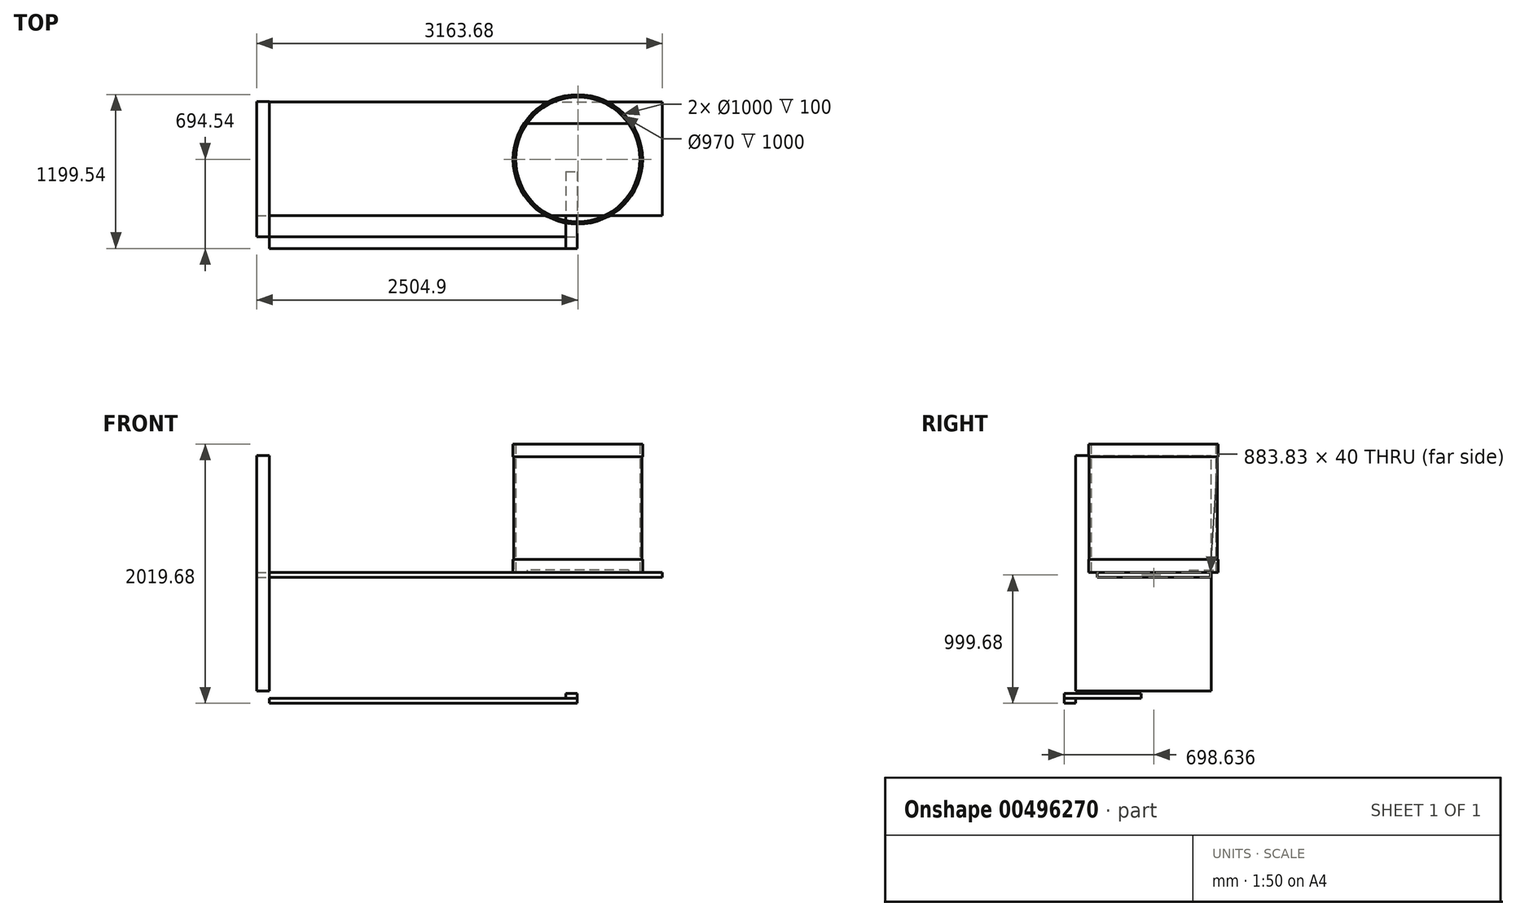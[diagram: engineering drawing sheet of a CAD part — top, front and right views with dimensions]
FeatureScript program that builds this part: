
annotation { "Feature Type Name" : "Feature", "Feature Type Description" : "" }
export const myFeature = defineFeature(function(context is Context, id is Id, definition is map)
    precondition{}
    {
        {
            var Q0;
            Q0=qCreatedBy(makeId("Top.planeOp"),FACE);
            var sketch = newSketch(context, id + "F0", { "sketchPlane" : qUnion([Q0])});
            skCircle(sketch, "E0", {"center": v(0, 0) * mm, "radius": 500 * mm});
            skSolve(sketch);
        }
        {
            var Q0;
            Q0=qSketchRegion(id+"F0",true);
            var sketch = newSketch(context, id + "F1", { "sketchPlane" : qUnion([Q0])});
            skCircle(sketch, "E1.0", {"center": v(0, 0) * mm, "radius": 485 * mm});
            skSolve(sketch);
        }
        {
            var Q0;
            Q0=qSketchRegion(id+"F0",true);
            var sketch = newSketch(context, id + "F2", { "sketchPlane" : qUnion([Q0])});
            skSolve(sketch);
        }
        {
            var Q0;
            Q0=makeQuery(id+"F1.imprint","IMPRINT",FACE,{"disambiguationData":[TD([[makeQuery(id+"F1.imprint","IMPRINT",EDGE,{"derivedFrom":sQuery(id+"F1.wireOp",EDGE,"E1.0")}),-1.0]])]});
            extrude(context, id + "F3", {"entities" : qUnion([Q0]), "depth" : 1000 * mm});
        }
        {
            var Q0;
            Q0=makeQuery(id+"F3.opExtrude","CAP_FACE",FACE,{"disambiguationData":[OSD([sQuery(id+"F0.wireOp",EDGE,"E0"),sQuery(id+"F1.wireOp",EDGE,"E1.0")])],"isStart":false});
            var sketch = newSketch(context, id + "F4", { "sketchPlane" : qUnion([Q0])});
            skCircle(sketch, "E2.0", {"center": v(0, 0) * mm, "radius": 505 * mm});
            skSolve(sketch);
        }
        {
            var Q0;
            Q0=makeQuery(id+"F4.imprint","IMPRINT",FACE,{"disambiguationData":[TD([[makeQuery(id+"F4.imprint","IMPRINT",EDGE,{"derivedFrom":sQuery(id+"F4.wireOp",EDGE,"E2.0")}),1.0]])]});
            var Q1;
            Q1=sQuery(id+"F4.wireOp",EDGE,"E2.0");
            extrude(context, id + "F5", {"entities" : qUnion([Q0]), "surfaceEntities" : qUnion([Q1]), "oppositeDirection" : true, "depth" : 100 * mm});
        }
        {
            var Q0;
            Q0=qSketchRegion(id+"F0",true);
            var sketch = newSketch(context, id + "F6", { "sketchPlane" : qUnion([Q0])});
            skCircle(sketch, "E3.0", {"center": v(0, 0) * mm, "radius": 505 * mm});
            skSolve(sketch);
        }
        {
            var Q0;
            Q0=makeQuery(id+"F6.imprint","IMPRINT",FACE,{"disambiguationData":[TD([[makeQuery(id+"F6.imprint","IMPRINT",EDGE,{"derivedFrom":sQuery(id+"F6.wireOp",EDGE,"E3.0")}),1.0]])]});
            var Q1;
            Q1=sQuery(id+"F6.wireOp",EDGE,"E3.0");
            var Q2;
            Q2=sQuery(id+"F0.wireOp",EDGE,"E0");
            extrude(context, id + "F7", {"entities" : qUnion([Q0]), "surfaceEntities" : qUnion([Q1, Q2]), "depth" : 100 * mm});
        }
        {
            var Q0;
            Q0=makeQuery(id+"F2.imprint","IMPRINT",FACE,{"disambiguationData":[TD([[makeQuery(id+"F2.imprint","IMPRINT",EDGE,{"derivedFrom":makeQuery(id+"F0.imprint","IMPRINT",EDGE,{"derivedFrom":sQuery(id+"F0.wireOp",EDGE,"E0")})}),1.0]])]});
            var sketch = newSketch(context, id + "F8", { "sketchPlane" : qUnion([Q0])});
            skLineSegment(sketch, "E4.0", {"start": v(-670.82, -280) * mm, "end": v(736.95, -280) * mm, "construction": true});
            skLineSegment(sketch, "E5.0", {"start": v(-280, 280) * mm, "end": v(736.95, 280) * mm, "construction": true});
            skLineSegment(sketch, "E6.0", {"start": v(-280, 280) * mm, "end": v(-280, -540.65) * mm, "construction": true});
            skLineSegment(sketch, "E7.0", {"start": v(280, 677.08) * mm, "end": v(280, -540.65) * mm, "construction": true});
            skCircle(sketch, "E8", {"center": v(392.31, 0) * mm, "radius": 25 * mm, "construction": true});
            skCircle(sketch, "E9", {"center": v(-397.36, 0) * mm, "radius": 25 * mm, "construction": true});
            skPoint(sketch, "E10.orphan", {"position": v(-670.82, 0) * mm});
            skPoint(sketch, "E11.orphan", {"position": v(0, 677.08) * mm});
            skLineSegment(sketch, "E12", {"start": v(-280, 210.88) * mm, "end": v(-280, 476.58) * mm});
            skLineSegment(sketch, "E13", {"start": v(-280, 280) * mm, "end": v(-559.63, 280) * mm});
            skSolve(sketch);
        }
        {
            var Q0;
            {var subQ0=sQuery(id+"F8.wireOp",EDGE,"E13");var subQ1=sQuery(id+"F8.wireOp",EDGE,"E12");var subQ2=makeQuery(id+"F8.imprint","INTERSECT",VERTEX,{"derivedFrom":[subQ1,subQ0]});Q0=makeQuery(id+"F8.imprint","IMPRINT",FACE,{"disambiguationData":[TD([[makeQuery(id+"F8.imprint","IMPRINT",EDGE,{"disambiguationData":[TD([[subQ2,-1.0]])],"derivedFrom":subQ1}),-1.0]])]});}
            var sketch = newSketch(context, id + "F9", { "sketchPlane" : qUnion([Q0])});
            skLineSegment(sketch, "E14", {"start": v(737.94, 279) * mm, "end": v(-365.76, 279) * mm});
            skLineSegment(sketch, "E15", {"start": v(-365.76, 279) * mm, "end": v(-460.28, 279) * mm});
            skArc(sketch, "E16", {"start": v(396.86, 279) * mm, "mid": v(0, 485.12) * mm, "end": v(-396.86, 279) * mm});
            skSolve(sketch);
        }
        {
            var Q0;
            Q0=qSketchRegion(id+"F9",true);
            extrude(context, id + "F10", {"entities" : qUnion([Q0]), "depth" : 20 * mm});
        }
        {
            var Q0;
            Q0=makeQuery(id+"F2.imprint","IMPRINT",FACE,{"disambiguationData":[TD([[makeQuery(id+"F2.imprint","IMPRINT",EDGE,{"derivedFrom":makeQuery(id+"F0.imprint","IMPRINT",EDGE,{"derivedFrom":sQuery(id+"F0.wireOp",EDGE,"E0")})}),1.0]])]});
            var sketch = newSketch(context, id + "F11", { "sketchPlane" : qUnion([Q0])});
            skLineSegment(sketch, "E17.bottom", {"start": v(-2404.9, -437.82) * mm, "end": v(658.78, -437.82) * mm});
            skLineSegment(sketch, "E17.top", {"start": v(-2404.9, 446) * mm, "end": v(658.78, 446) * mm});
            skLineSegment(sketch, "E17.left", {"start": v(-2404.9, -437.82) * mm, "end": v(-2404.9, 446) * mm});
            skLineSegment(sketch, "E17.right", {"start": v(658.78, -437.82) * mm, "end": v(658.78, 446) * mm});
            skSolve(sketch);
        }
        {
            var Q0;
            Q0=qSketchRegion(id+"F11",true);
            extrude(context, id + "F12", {"entities" : qUnion([Q0]), "oppositeDirection" : true, "depth" : 40 * mm});
        }
        {
            var Q0;
            Q0=makeQuery(id+"F12.opExtrude","SWEPT_FACE",FACE,{"disambiguationData":[OSD([sQuery(id+"F11.wireOp",EDGE,"E17.left")])]});
            var sketch = newSketch(context, id + "F13", { "sketchPlane" : qUnion([Q0])});
            skLineSegment(sketch, "E18.bottom", {"start": v(604.54, -923.26) * mm, "end": v(-449.95, -923.26) * mm});
            skLineSegment(sketch, "E18.top", {"start": v(604.54, 909.63) * mm, "end": v(-449.95, 909.63) * mm});
            skLineSegment(sketch, "E18.left", {"start": v(604.54, -923.26) * mm, "end": v(604.54, 909.63) * mm});
            skLineSegment(sketch, "E18.right", {"start": v(-449.95, -923.26) * mm, "end": v(-449.95, 909.63) * mm});
            skSolve(sketch);
        }
        {
            var Q0;
            Q0=makeQuery(id+"F13.imprint","IMPRINT",FACE,{"disambiguationData":[TD([[makeQuery(id+"F13.imprint","IMPRINT",EDGE,{"derivedFrom":sQuery(id+"F13.wireOp",EDGE,"E18.bottom")}),-1.0]])]});
            extrude(context, id + "F14", {"entities" : qUnion([Q0]), "depth" : 100 * mm});
        }
        {
            var Q0;
            Q0=makeQuery(id+"F14.opExtrude","SWEPT_FACE",FACE,{"disambiguationData":[OSD([sQuery(id+"F13.wireOp",EDGE,"E18.left")])]});
            var sketch = newSketch(context, id + "F15", { "sketchPlane" : qUnion([Q0])});
            skLineSegment(sketch, "E19.bottom", {"start": v(-2404.9, -981.68) * mm, "end": v(-4.9, -981.68) * mm});
            skLineSegment(sketch, "E19.top", {"start": v(-2404.9, -1019.68) * mm, "end": v(-4.9, -1019.68) * mm});
            skLineSegment(sketch, "E19.left", {"start": v(-2404.9, -981.68) * mm, "end": v(-2404.9, -1019.68) * mm});
            skLineSegment(sketch, "E19.right", {"start": v(-4.9, -981.68) * mm, "end": v(-4.9, -1019.68) * mm});
            skSolve(sketch);
        }
        {
            var Q0;
            Q0=qSketchRegion(id+"F15",true);
            extrude(context, id + "F16", {"entities" : qUnion([Q0]), "depth" : 90 * mm});
        }
        {
            var Q0;
            Q0=makeQuery(id+"F16.opExtrude","CAP_FACE",FACE,{"disambiguationData":[OSD([sQuery(id+"F15.wireOp",EDGE,"E19.bottom"),sQuery(id+"F15.wireOp",EDGE,"E19.top"),sQuery(id+"F15.wireOp",EDGE,"E19.left"),sQuery(id+"F15.wireOp",EDGE,"E19.right")])],"isStart":false});
            var sketch = newSketch(context, id + "F17", { "sketchPlane" : qUnion([Q0])});
            skLineSegment(sketch, "E20.bottom", {"start": v(-4.9, -981.68) * mm, "end": v(-94.9, -981.68) * mm});
            skLineSegment(sketch, "E20.top", {"start": v(-4.9, -942.68) * mm, "end": v(-94.9, -942.68) * mm});
            skLineSegment(sketch, "E20.left", {"start": v(-4.9, -981.68) * mm, "end": v(-4.9, -942.68) * mm});
            skLineSegment(sketch, "E20.right", {"start": v(-94.9, -981.68) * mm, "end": v(-94.9, -942.68) * mm});
            skSolve(sketch);
        }
        {
            var Q0;
            Q0=qSketchRegion(id+"F17",true);
            extrude(context, id + "F18", {"entities" : qUnion([Q0]), "oppositeDirection" : true, "depth" : 600 * mm});
        }
    });
